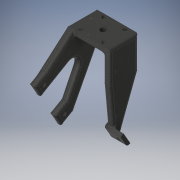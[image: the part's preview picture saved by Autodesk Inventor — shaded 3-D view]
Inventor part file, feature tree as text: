
AUTODESK INVENTOR PART (.ipt)
format: ipt  version: 2019.4 (Build 234330000, 330)  size: 540,672 bytes
history: native  units: mm
features: fillet x11, extrude x8, sketch x8
ambient origin geometry x8: Origin, YZ Plane, XZ Plane, XY Plane, X Axis, Y Axis, Z Axis, Center Point
bodies: Solid1 (feature_tree)
feature tree (27):
  extrude  "Extrusion1"  Depth=42.3mm
  extrude  "Extrusion2"  Depth=10.0mm
  sketch  "Sketch3"  dims[d5=42.3mm d6=15.0mm d7=0.0mm]
  extrude  "Extrusion4"  Depth=15.0mm TaperAngle=0.0deg
  extrude  "Extrusion10"  Depth=5.65mm
  fillet  "Fillet2"  Radius=3.5mm
  fillet  "Fillet3"  Radius=21.15mm
  fillet  "Fillet4"  Radius=8.0mm
  fillet  "Fillet5"  Radius=10.0mm
  fillet  "Fillet7"  Radius=12.2mm
  fillet  "Fillet8"  Radius=100.0mm
  extrude  "Extrusion12"  Depth=10.0mm
  extrude  "Extrusion13"  Depth=20.0mm
  extrude  "Extrusion14"  Depth=20.0mm
  fillet  "Fillet9"  Radius=30.0mm
  fillet  "Fillet10"  Radius=5.5mm
  fillet  "Fillet11"  Radius=20.0mm
  fillet  "Fillet12"  [1 undecoded]
  extrude  "Extrusion15"  Depth=20.0mm
  fillet  "Fillet13"  Radius=20.0mm
  sketch  "Sketch1"  dims[d0=52.3mm d1=42.3mm]
  sketch  "Sketch2"  dims[d2=7.0mm d3=0.0mm d4=10.0mm]
  sketch  "Sketch4"  dims[d8=5.65mm d9=5.65mm d10=3.5mm]
  sketch  "Sketch9"  dims[d11=20.0mm d13=31.0mm d14=20.0mm d16=31.0mm d21=21.15mm d22=8.0mm d23=10.0mm d24=0.0mm d77=12.2mm d78=100.0mm]
  sketch  "Sketch12"  dims[d79=60.0deg d80=10.0mm]
  sketch  "Sketch13"  dims[d81=90.0deg d82=20.0mm]
  sketch  "Sketch14"  dims[d83=60.0deg d84=20.0mm d85=30.0mm d88=5.5mm d90=20.0mm d91=60.0deg d92=20.0mm d103=20.0mm d105=60.0mm d106=10.0mm d108=10.0mm d110=10.0mm d111=0.0mm d112=10.0mm d113=2.0mm d114=4.0mm d115=4.0mm d117=4.0mm d118=2.0mm d131=29.994mm d132=60.0deg d133=9.995mm d134=1.0mm d135=30.0deg d136=19.99mm d137=120.0deg d138=5.0mm d139=42.3mm d140=40.0mm d141=10.0mm d142=0.0mm d143=15.0mm d144=0.0mm d145=8.0mm d146=5.1mm d147=5.0mm d148=0.0mm d149=4.0mm d150=4.0mm d151=4.0mm d152=4.0mm d153=1.5mm d155=10.0mm d156=1.5mm d157=3.5mm d158=20.0mm d160=34.0mm d161=20.0mm d163=34.0mm d166=15.0mm d167=0.0mm d168=2.0mm]
note: 1 required parameter value undecoded (feature->parameter linkage not recoverable at this tier; creation-order binding heuristic only, values carry confidence <= 0.55)
